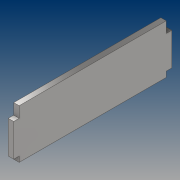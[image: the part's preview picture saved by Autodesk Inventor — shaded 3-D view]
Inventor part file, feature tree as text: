
AUTODESK INVENTOR PART (.ipt)
format: ipt  version: 2021 (Build 250183000, 183)  size: 119,296 bytes
history: native  units: mm
features: extrude x2, sketch x2, projected_geometry x1
ambient origin geometry x8: Origin, YZ Plane, XZ Plane, XY Plane, X Axis, Y Axis, Z Axis, Center Point
bodies: Solid1 (feature_tree)
feature tree (5):
  extrude  "Extrusion1"  Depth=270.0mm
  extrude  "Extrusion2"  Depth=10.0mm TaperAngle=0.0deg
  sketch  "Sketch1"  dims[d0=90.0mm d1=270.0mm]
  sketch  "Sketch2"  dims[d2=10.0mm d3=0.0mm d6=10.0mm d7=0.0mm d8=90.0mm d9=50.0mm d10=60.0mm d11=290.0mm d12=270.0mm]
  projected_geometry  "Projected Loop1"
